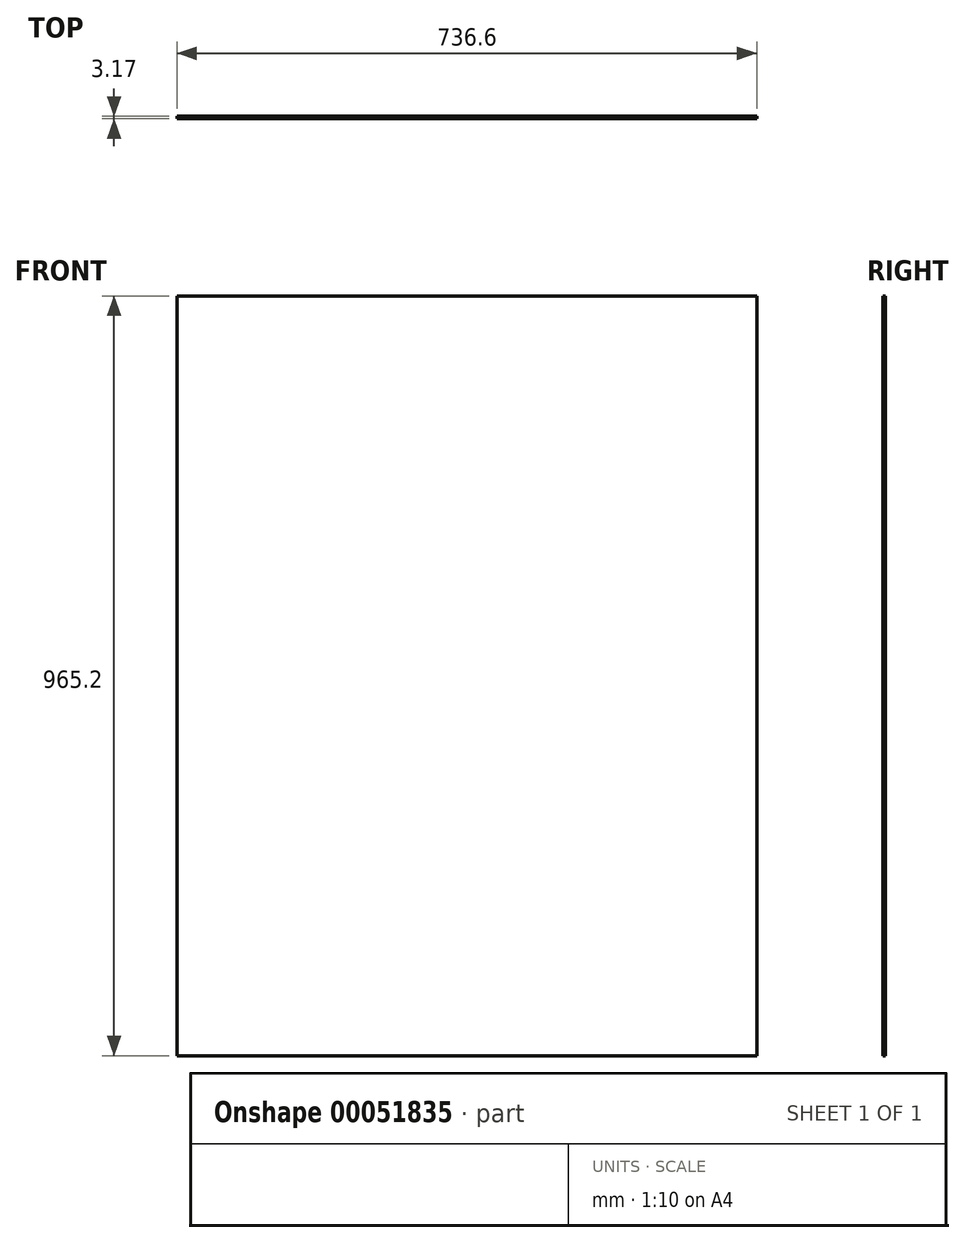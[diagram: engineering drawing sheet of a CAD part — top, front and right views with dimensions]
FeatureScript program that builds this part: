
annotation { "Feature Type Name" : "Feature", "Feature Type Description" : "" }
export const myFeature = defineFeature(function(context is Context, id is Id, definition is map)
    precondition{}
    {
        {
            var Q0;
            Q0=qCreatedBy(makeId("Front.planeOp"),FACE);
            var sketch = newSketch(context, id + "F0", { "sketchPlane" : qUnion([Q0])});
            skLineSegment(sketch, "E0.bottom", {"start": v(-368.3, -482.6) * mm, "end": v(368.3, -482.6) * mm});
            skLineSegment(sketch, "E0.top", {"start": v(-368.3, 482.6) * mm, "end": v(368.3, 482.6) * mm});
            skLineSegment(sketch, "E0.left", {"start": v(-368.3, -482.6) * mm, "end": v(-368.3, 482.6) * mm});
            skLineSegment(sketch, "E0.right", {"start": v(368.3, -482.6) * mm, "end": v(368.3, 482.6) * mm});
            skSolve(sketch);
        }
        {
            var Q0;
            Q0=makeQuery(id+"F0.imprint","IMPRINT",FACE,{"disambiguationData":[TD([[makeQuery(id+"F0.imprint","IMPRINT",EDGE,{"derivedFrom":sQuery(id+"F0.wireOp",EDGE,"E0.bottom")}),1.0]])]});
            extrude(context, id + "F1", {"entities" : qUnion([Q0]), "depth" : 3.17 * mm});
        }
    });
